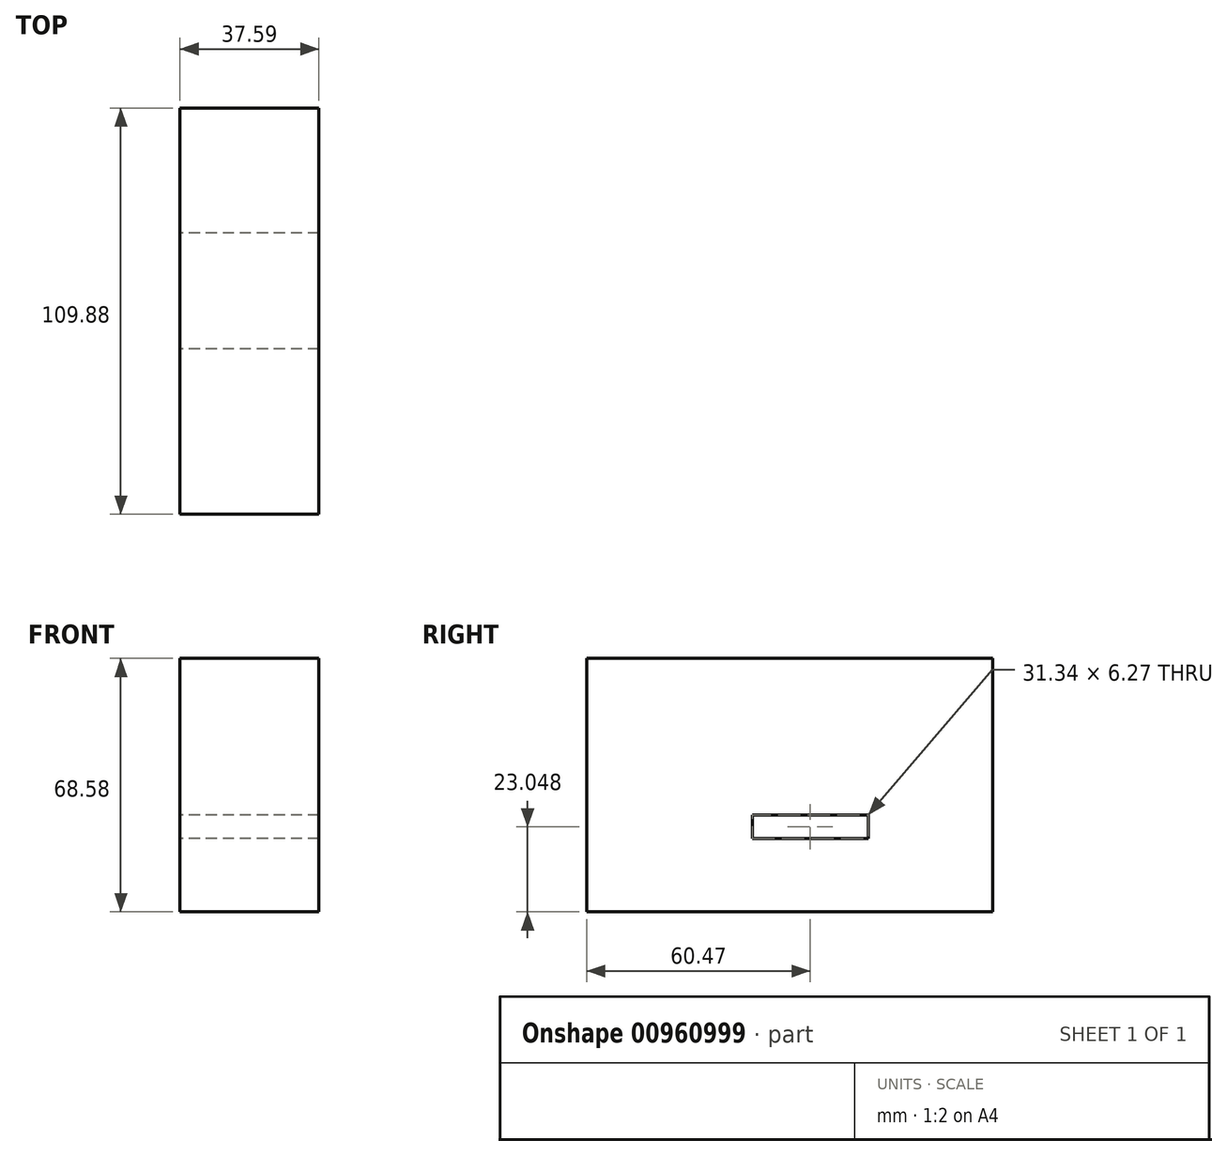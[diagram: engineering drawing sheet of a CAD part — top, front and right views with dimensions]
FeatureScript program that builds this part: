
annotation { "Feature Type Name" : "Feature", "Feature Type Description" : "" }
export const myFeature = defineFeature(function(context is Context, id is Id, definition is map)
    precondition{}
    {
        {
            var Q0;
            Q0=qCreatedBy(makeId("Right.planeOp"),FACE);
            var sketch = newSketch(context, id + "F0", { "sketchPlane" : qUnion([Q0])});
            skLineSegment(sketch, "E0.bottom", {"start": v(-49.87, 50.97) * mm, "end": v(60, 50.97) * mm});
            skLineSegment(sketch, "E0.top", {"start": v(-49.87, -17.6) * mm, "end": v(60, -17.6) * mm});
            skLineSegment(sketch, "E0.left", {"start": v(-49.87, 50.97) * mm, "end": v(-49.87, -17.6) * mm});
            skLineSegment(sketch, "E0.right", {"start": v(60, 50.97) * mm, "end": v(60, -17.6) * mm});
            skLineSegment(sketch, "E1.bottom", {"start": v(-5.07, 8.57) * mm, "end": v(26.27, 8.57) * mm});
            skLineSegment(sketch, "E1.top", {"start": v(-5.07, 2.3) * mm, "end": v(26.27, 2.3) * mm});
            skLineSegment(sketch, "E1.left", {"start": v(-5.07, 8.57) * mm, "end": v(-5.07, 2.3) * mm});
            skLineSegment(sketch, "E1.right", {"start": v(26.27, 8.57) * mm, "end": v(26.27, 2.3) * mm});
            skSolve(sketch);
        }
        {
            var Q0;
            Q0 = qSketchRegion(id + "F0", true);
            extrude(context, id + "F1", {"entities" : qUnion([Q0]), "depth" : 37.6 * mm, "offsetDistance" : 25.4 * mm});
        }
    });
